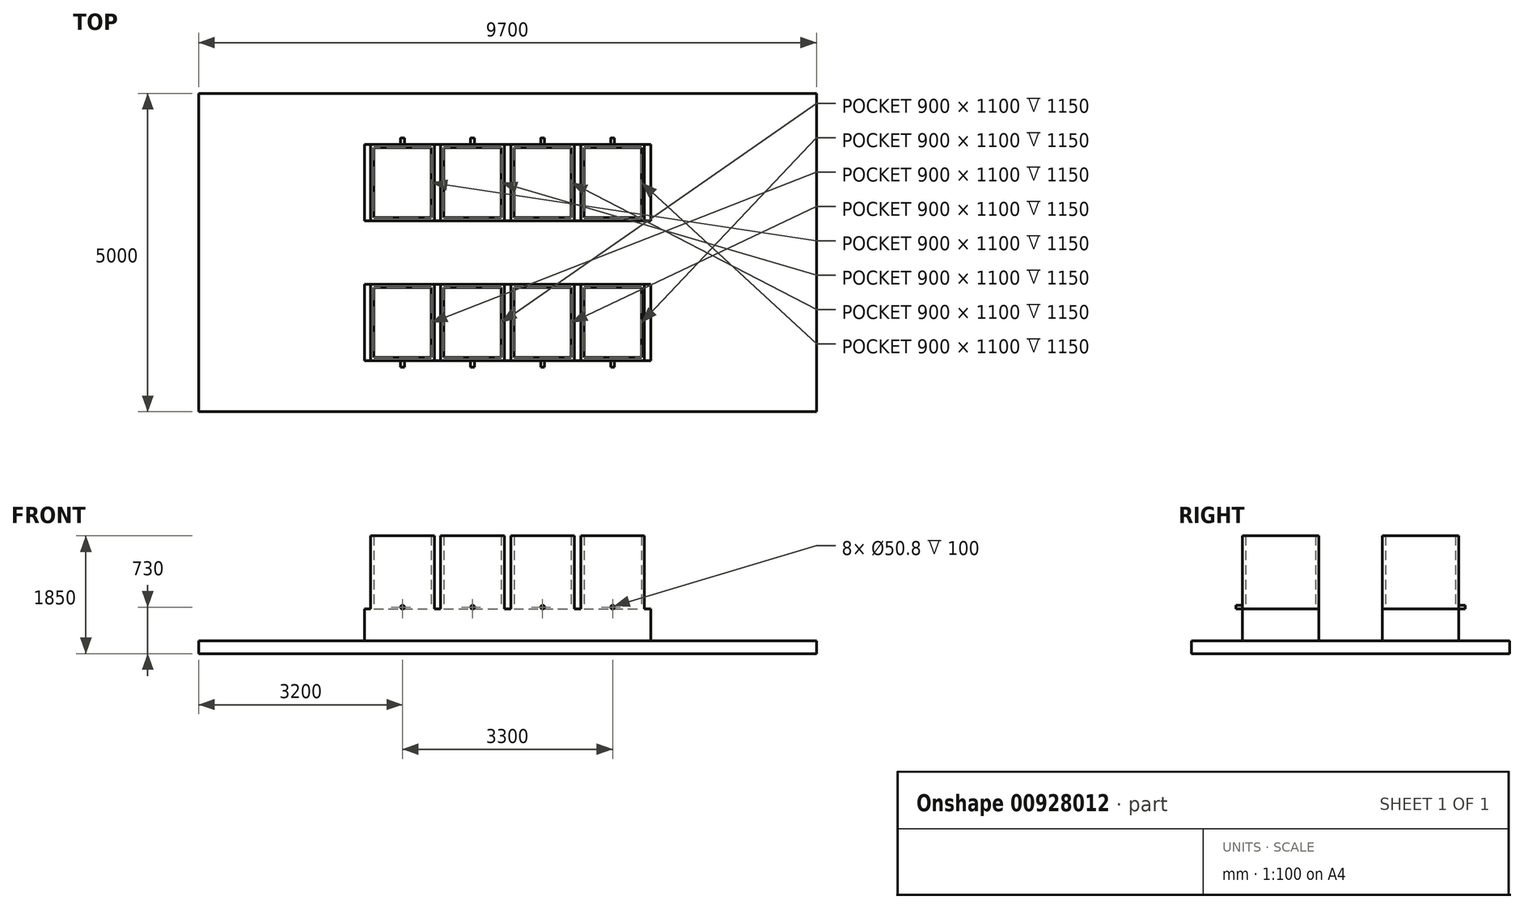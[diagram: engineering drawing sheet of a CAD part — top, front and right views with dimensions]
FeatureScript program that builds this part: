
annotation { "Feature Type Name" : "Feature", "Feature Type Description" : "" }
export const myFeature = defineFeature(function(context is Context, id is Id, definition is map)
    precondition{}
    {
        {
            var Q0;
            Q0=qCreatedBy(makeId("Top.planeOp"),FACE);
            var sketch = newSketch(context, id + "F0", { "sketchPlane" : qUnion([Q0])});
            skLineSegment(sketch, "E0.bottom", {"start": v(0, 0) * mm, "end": v(9700, 0) * mm});
            skLineSegment(sketch, "E0.top", {"start": v(0, 5000) * mm, "end": v(9700, 5000) * mm});
            skLineSegment(sketch, "E0.left", {"start": v(0, 0) * mm, "end": v(0, 5000) * mm});
            skLineSegment(sketch, "E0.right", {"start": v(9700, 0) * mm, "end": v(9700, 5000) * mm});
            skSolve(sketch);
        }
        {
            var Q0;
            Q0 = qSketchRegion(id + "F0", true);
            extrude(context, id + "F1", {"entities" : qUnion([Q0]), "depth" : 200 * mm, "offsetDistance" : 25 * mm});
        }
        {
            var Q0;
            Q0=makeQuery(id+"F1.opExtrude","CAP_FACE",FACE,{"disambiguationData":[OSD([sQuery(id+"F0.wireOp",EDGE,"E0.bottom"),sQuery(id+"F0.wireOp",EDGE,"E0.top"),sQuery(id+"F0.wireOp",EDGE,"E0.left"),sQuery(id+"F0.wireOp",EDGE,"E0.right")])],"isStart":false});
            var sketch = newSketch(context, id + "F2", { "sketchPlane" : qUnion([Q0])});
            skLineSegment(sketch, "E1.0", {"start": v(0, 0) * mm, "end": v(0, 5000) * mm});
            skLineSegment(sketch, "E1.1", {"start": v(0, 5000) * mm, "end": v(9700, 5000) * mm});
            skLineSegment(sketch, "E1.2", {"start": v(9700, 0) * mm, "end": v(9700, 5000) * mm});
            skLineSegment(sketch, "E1.3", {"start": v(0, 0) * mm, "end": v(9700, 0) * mm});
            skLineSegment(sketch, "E2.bottom", {"start": v(2600, 4200) * mm, "end": v(7100, 4200) * mm});
            skLineSegment(sketch, "E2.top", {"start": v(2600, 3000) * mm, "end": v(7100, 3000) * mm});
            skLineSegment(sketch, "E2.left", {"start": v(2600, 4200) * mm, "end": v(2600, 3000) * mm});
            skLineSegment(sketch, "E2.right", {"start": v(7100, 4200) * mm, "end": v(7100, 3000) * mm});
            skLineSegment(sketch, "E3.bottom", {"start": v(2600, 2000) * mm, "end": v(7100, 2000) * mm});
            skLineSegment(sketch, "E3.top", {"start": v(2600, 800) * mm, "end": v(7100, 800) * mm});
            skLineSegment(sketch, "E3.left", {"start": v(2600, 2000) * mm, "end": v(2600, 800) * mm});
            skLineSegment(sketch, "E3.right", {"start": v(7100, 2000) * mm, "end": v(7100, 800) * mm});
            skLineSegment(sketch, "E4", {"start": v(0, 2500) * mm, "end": v(9700, 2500) * mm, "construction": true});
            skSolve(sketch);
        }
        {
            var Q0;
            Q0=makeQuery(id+"F2.imprint","IMPRINT",FACE,{"disambiguationData":[TD([[makeQuery(id+"F2.imprint","IMPRINT",EDGE,{"derivedFrom":sQuery(id+"F2.wireOp",EDGE,"E3.bottom")}),-1.0]])]});
            var Q1;
            Q1=makeQuery(id+"F2.imprint","IMPRINT",FACE,{"disambiguationData":[TD([[makeQuery(id+"F2.imprint","IMPRINT",EDGE,{"derivedFrom":sQuery(id+"F2.wireOp",EDGE,"E2.bottom")}),-1.0]])]});
            extrude(context, id + "F3", {"entities" : qUnion([Q0, Q1]), "operationType" : NewBodyOperationType.ADD, "depth" : 500 * mm, "offsetDistance" : 25 * mm});
        }
        {
            var Q0;
            Q0=makeQuery(id+"F3.opExtrude","CAP_FACE",FACE,{"disambiguationData":[OSD([sQuery(id+"F2.wireOp",EDGE,"E3.bottom"),sQuery(id+"F2.wireOp",EDGE,"E3.top"),sQuery(id+"F2.wireOp",EDGE,"E3.left"),sQuery(id+"F2.wireOp",EDGE,"E3.right")])],"isStart":false});
            var sketch = newSketch(context, id + "F4", { "sketchPlane" : qUnion([Q0])});
            skLineSegment(sketch, "E5.bottom", {"start": v(2700, 4200) * mm, "end": v(3700, 4200) * mm});
            skLineSegment(sketch, "E5.top", {"start": v(2700, 3000) * mm, "end": v(3700, 3000) * mm});
            skLineSegment(sketch, "E5.left", {"start": v(2700, 4200) * mm, "end": v(2700, 3000) * mm});
            skLineSegment(sketch, "E5.right", {"start": v(3700, 4200) * mm, "end": v(3700, 3000) * mm});
            skLineSegment(sketch, "E6.bottom", {"start": v(3800, 4200) * mm, "end": v(4800, 4200) * mm});
            skLineSegment(sketch, "E6.top", {"start": v(3800, 3000) * mm, "end": v(4800, 3000) * mm});
            skLineSegment(sketch, "E6.left", {"start": v(3800, 4200) * mm, "end": v(3800, 3000) * mm});
            skLineSegment(sketch, "E6.right", {"start": v(4800, 4200) * mm, "end": v(4800, 3000) * mm});
            skLineSegment(sketch, "E7.bottom", {"start": v(4900, 4200) * mm, "end": v(5900, 4200) * mm});
            skLineSegment(sketch, "E7.top", {"start": v(4900, 3000) * mm, "end": v(5900, 3000) * mm});
            skLineSegment(sketch, "E7.left", {"start": v(4900, 4200) * mm, "end": v(4900, 3000) * mm});
            skLineSegment(sketch, "E7.right", {"start": v(5900, 4200) * mm, "end": v(5900, 3000) * mm});
            skLineSegment(sketch, "E8.bottom", {"start": v(6000, 4200) * mm, "end": v(7000, 4200) * mm});
            skLineSegment(sketch, "E8.top", {"start": v(6000, 3000) * mm, "end": v(7000, 3000) * mm});
            skLineSegment(sketch, "E8.left", {"start": v(6000, 4200) * mm, "end": v(6000, 3000) * mm});
            skLineSegment(sketch, "E8.right", {"start": v(7000, 4200) * mm, "end": v(7000, 3000) * mm});
            skLineSegment(sketch, "E9.0", {"start": v(0, 2500) * mm, "end": v(9700, 2500) * mm, "construction": true});
            skLineSegment(sketch, "E10.MirrorCS", {"start": v(4800, 800) * mm, "end": v(4800, 2000) * mm});
            skLineSegment(sketch, "E11.MirrorCS", {"start": v(6000, 800) * mm, "end": v(6000, 2000) * mm});
            skLineSegment(sketch, "E12.MirrorCS", {"start": v(2700, 800) * mm, "end": v(2700, 2000) * mm});
            skLineSegment(sketch, "E13.MirrorCS", {"start": v(5900, 800) * mm, "end": v(5900, 2000) * mm});
            skLineSegment(sketch, "E14.MirrorCS", {"start": v(6000, 800) * mm, "end": v(7000, 800) * mm});
            skLineSegment(sketch, "E15.MirrorCS", {"start": v(4900, 2000) * mm, "end": v(5900, 2000) * mm});
            skLineSegment(sketch, "E16.MirrorCS", {"start": v(3700, 800) * mm, "end": v(3700, 2000) * mm});
            skLineSegment(sketch, "E17.MirrorCS", {"start": v(6000, 2000) * mm, "end": v(7000, 2000) * mm});
            skLineSegment(sketch, "E18.MirrorCS", {"start": v(4900, 800) * mm, "end": v(4900, 2000) * mm});
            skLineSegment(sketch, "E19.MirrorCS", {"start": v(2700, 800) * mm, "end": v(3700, 800) * mm});
            skLineSegment(sketch, "E20.MirrorCS", {"start": v(2700, 2000) * mm, "end": v(3700, 2000) * mm});
            skLineSegment(sketch, "E21.MirrorCS", {"start": v(3800, 2000) * mm, "end": v(4800, 2000) * mm});
            skLineSegment(sketch, "E22.MirrorCS", {"start": v(4900, 800) * mm, "end": v(5900, 800) * mm});
            skLineSegment(sketch, "E23.MirrorCS", {"start": v(3800, 800) * mm, "end": v(4800, 800) * mm});
            skLineSegment(sketch, "E24.MirrorCS", {"start": v(3800, 800) * mm, "end": v(3800, 2000) * mm});
            skLineSegment(sketch, "E25.MirrorCS", {"start": v(7000, 800) * mm, "end": v(7000, 2000) * mm});
            skLineSegment(sketch, "E26.bottom", {"start": v(2750, 4150) * mm, "end": v(3650, 4150) * mm});
            skLineSegment(sketch, "E26.top", {"start": v(2750, 3050) * mm, "end": v(3650, 3050) * mm});
            skLineSegment(sketch, "E26.left", {"start": v(2750, 4150) * mm, "end": v(2750, 3050) * mm});
            skLineSegment(sketch, "E26.right", {"start": v(3650, 4150) * mm, "end": v(3650, 3050) * mm});
            skLineSegment(sketch, "E27.bottom", {"start": v(3850, 4150) * mm, "end": v(4750, 4150) * mm});
            skLineSegment(sketch, "E27.top", {"start": v(3850, 3050) * mm, "end": v(4750, 3050) * mm});
            skLineSegment(sketch, "E27.left", {"start": v(3850, 4150) * mm, "end": v(3850, 3050) * mm});
            skLineSegment(sketch, "E27.right", {"start": v(4750, 4150) * mm, "end": v(4750, 3050) * mm});
            skLineSegment(sketch, "E28.bottom", {"start": v(4950, 4150) * mm, "end": v(5850, 4150) * mm});
            skLineSegment(sketch, "E28.top", {"start": v(4950, 3050) * mm, "end": v(5850, 3050) * mm});
            skLineSegment(sketch, "E28.left", {"start": v(4950, 4150) * mm, "end": v(4950, 3050) * mm});
            skLineSegment(sketch, "E28.right", {"start": v(5850, 4150) * mm, "end": v(5850, 3050) * mm});
            skLineSegment(sketch, "E29.bottom", {"start": v(6050, 4150) * mm, "end": v(6950, 4150) * mm});
            skLineSegment(sketch, "E29.top", {"start": v(6050, 3050) * mm, "end": v(6950, 3050) * mm});
            skLineSegment(sketch, "E29.left", {"start": v(6050, 4150) * mm, "end": v(6050, 3050) * mm});
            skLineSegment(sketch, "E29.right", {"start": v(6950, 4150) * mm, "end": v(6950, 3050) * mm});
            skLineSegment(sketch, "E30.bottom", {"start": v(2750, 1950) * mm, "end": v(3650, 1950) * mm});
            skLineSegment(sketch, "E30.top", {"start": v(2750, 850) * mm, "end": v(3650, 850) * mm});
            skLineSegment(sketch, "E30.left", {"start": v(2750, 1950) * mm, "end": v(2750, 850) * mm});
            skLineSegment(sketch, "E30.right", {"start": v(3650, 1950) * mm, "end": v(3650, 850) * mm});
            skLineSegment(sketch, "E31.bottom", {"start": v(3850, 1950) * mm, "end": v(4750, 1950) * mm});
            skLineSegment(sketch, "E31.top", {"start": v(3850, 850) * mm, "end": v(4750, 850) * mm});
            skLineSegment(sketch, "E31.left", {"start": v(3850, 1950) * mm, "end": v(3850, 850) * mm});
            skLineSegment(sketch, "E31.right", {"start": v(4750, 1950) * mm, "end": v(4750, 850) * mm});
            skLineSegment(sketch, "E32.bottom", {"start": v(4950, 1950) * mm, "end": v(5850, 1950) * mm});
            skLineSegment(sketch, "E32.top", {"start": v(4950, 850) * mm, "end": v(5850, 850) * mm});
            skLineSegment(sketch, "E32.left", {"start": v(4950, 1950) * mm, "end": v(4950, 850) * mm});
            skLineSegment(sketch, "E32.right", {"start": v(5850, 1950) * mm, "end": v(5850, 850) * mm});
            skLineSegment(sketch, "E33.bottom", {"start": v(6050, 1950) * mm, "end": v(6950, 1950) * mm});
            skLineSegment(sketch, "E33.top", {"start": v(6050, 850) * mm, "end": v(6950, 850) * mm});
            skLineSegment(sketch, "E33.left", {"start": v(6050, 1950) * mm, "end": v(6050, 850) * mm});
            skLineSegment(sketch, "E33.right", {"start": v(6950, 1950) * mm, "end": v(6950, 850) * mm});
            skSolve(sketch);
        }
        {
            var Q0;
            Q0 = qSketchRegion(id + "F4", true);
            extrude(context, id + "F5", {"entities" : qUnion([Q0]), "depth" : 1150 * mm, "offsetDistance" : 25 * mm});
        }
        {
            var Q0;
            Q0=makeQuery(id+"F5.opExtrude","SWEPT_FACE",FACE,{"disambiguationData":[OSD([sQuery(id+"F4.wireOp",EDGE,"E19.MirrorCS")])]});
            var sketch = newSketch(context, id + "F6", { "sketchPlane" : qUnion([Q0])});
            skLineSegment(sketch, "E34", {"start": v(3200, 1850) * mm, "end": v(3200, 700) * mm, "construction": true});
            skLineSegment(sketch, "E35.0", {"start": v(3800, 1850) * mm, "end": v(4800, 1850) * mm, "construction": true});
            skLineSegment(sketch, "E35.1", {"start": v(4900, 1850) * mm, "end": v(5900, 1850) * mm, "construction": true});
            skLineSegment(sketch, "E35.2", {"start": v(6000, 1850) * mm, "end": v(7000, 1850) * mm, "construction": true});
            skLineSegment(sketch, "E36.0", {"start": v(2600, 700) * mm, "end": v(7100, 700) * mm, "construction": true});
            skLineSegment(sketch, "E37", {"start": v(4300, 1850) * mm, "end": v(4300, 700) * mm, "construction": true});
            skLineSegment(sketch, "E38", {"start": v(5400, 1850) * mm, "end": v(5400, 700) * mm, "construction": true});
            skLineSegment(sketch, "E39", {"start": v(6500, 1850) * mm, "end": v(6500, 700) * mm, "construction": true});
            skCircle(sketch, "E40", {"center": v(3200, 730) * mm, "radius": 30 * mm});
            skCircle(sketch, "E41", {"center": v(4300, 730) * mm, "radius": 30 * mm});
            skCircle(sketch, "E42", {"center": v(5400, 730) * mm, "radius": 30 * mm});
            skCircle(sketch, "E43", {"center": v(6500, 730) * mm, "radius": 30 * mm});
            skCircle(sketch, "E44", {"center": v(3200, 730) * mm, "radius": 25.4 * mm});
            skCircle(sketch, "E45", {"center": v(4300, 730) * mm, "radius": 25.4 * mm});
            skCircle(sketch, "E46", {"center": v(5400, 730) * mm, "radius": 25.4 * mm});
            skCircle(sketch, "E47", {"center": v(6500, 730) * mm, "radius": 25.4 * mm});
            skSolve(sketch);
        }
        {
            var Q0;
            Q0 = qSketchRegion(id + "F6", true);
            extrude(context, id + "F7", {"entities" : qUnion([Q0]), "operationType" : NewBodyOperationType.ADD, "depth" : 100 * mm, "offsetDistance" : 25 * mm});
        }
        {
            var Q0;
            Q0=makeQuery(id+"F5.opExtrude","SWEPT_FACE",FACE,{"disambiguationData":[OSD([sQuery(id+"F4.wireOp",EDGE,"E8.bottom")])]});
            var sketch = newSketch(context, id + "F8", { "sketchPlane" : qUnion([Q0])});
            skLineSegment(sketch, "E48.0", {"start": v(-6000, 1850) * mm, "end": v(-7000, 1850) * mm, "construction": true});
            skLineSegment(sketch, "E48.1", {"start": v(-4900, 1850) * mm, "end": v(-5900, 1850) * mm, "construction": true});
            skLineSegment(sketch, "E48.2", {"start": v(-3800, 1850) * mm, "end": v(-4800, 1850) * mm, "construction": true});
            skLineSegment(sketch, "E48.3", {"start": v(-2700, 1850) * mm, "end": v(-3700, 1850) * mm, "construction": true});
            skLineSegment(sketch, "E48.4", {"start": v(-2600, 700) * mm, "end": v(-7100, 700) * mm, "construction": true});
            skLineSegment(sketch, "E49", {"start": v(-6500, 1850) * mm, "end": v(-6500, 700) * mm, "construction": true});
            skLineSegment(sketch, "E50", {"start": v(-5400, 1850) * mm, "end": v(-5400, 700) * mm, "construction": true});
            skLineSegment(sketch, "E51", {"start": v(-4300, 1850) * mm, "end": v(-4300, 700) * mm, "construction": true});
            skLineSegment(sketch, "E52", {"start": v(-3200, 1850) * mm, "end": v(-3200, 700) * mm, "construction": true});
            skCircle(sketch, "E53", {"center": v(-6500, 730) * mm, "radius": 30 * mm});
            skCircle(sketch, "E54", {"center": v(-6500, 730) * mm, "radius": 25.4 * mm});
            skCircle(sketch, "E55", {"center": v(-5400, 730) * mm, "radius": 30 * mm});
            skCircle(sketch, "E56", {"center": v(-5400, 730) * mm, "radius": 25.4 * mm});
            skCircle(sketch, "E57", {"center": v(-4300, 730) * mm, "radius": 30 * mm});
            skCircle(sketch, "E58", {"center": v(-4300, 730) * mm, "radius": 25.4 * mm});
            skCircle(sketch, "E59", {"center": v(-3200, 730) * mm, "radius": 30 * mm});
            skCircle(sketch, "E60", {"center": v(-3200, 730) * mm, "radius": 25.4 * mm});
            skSolve(sketch);
        }
        {
            var Q0;
            Q0 = qSketchRegion(id + "F8", true);
            extrude(context, id + "F9", {"entities" : qUnion([Q0]), "operationType" : NewBodyOperationType.ADD, "depth" : 100 * mm, "offsetDistance" : 25 * mm});
        }
    });
